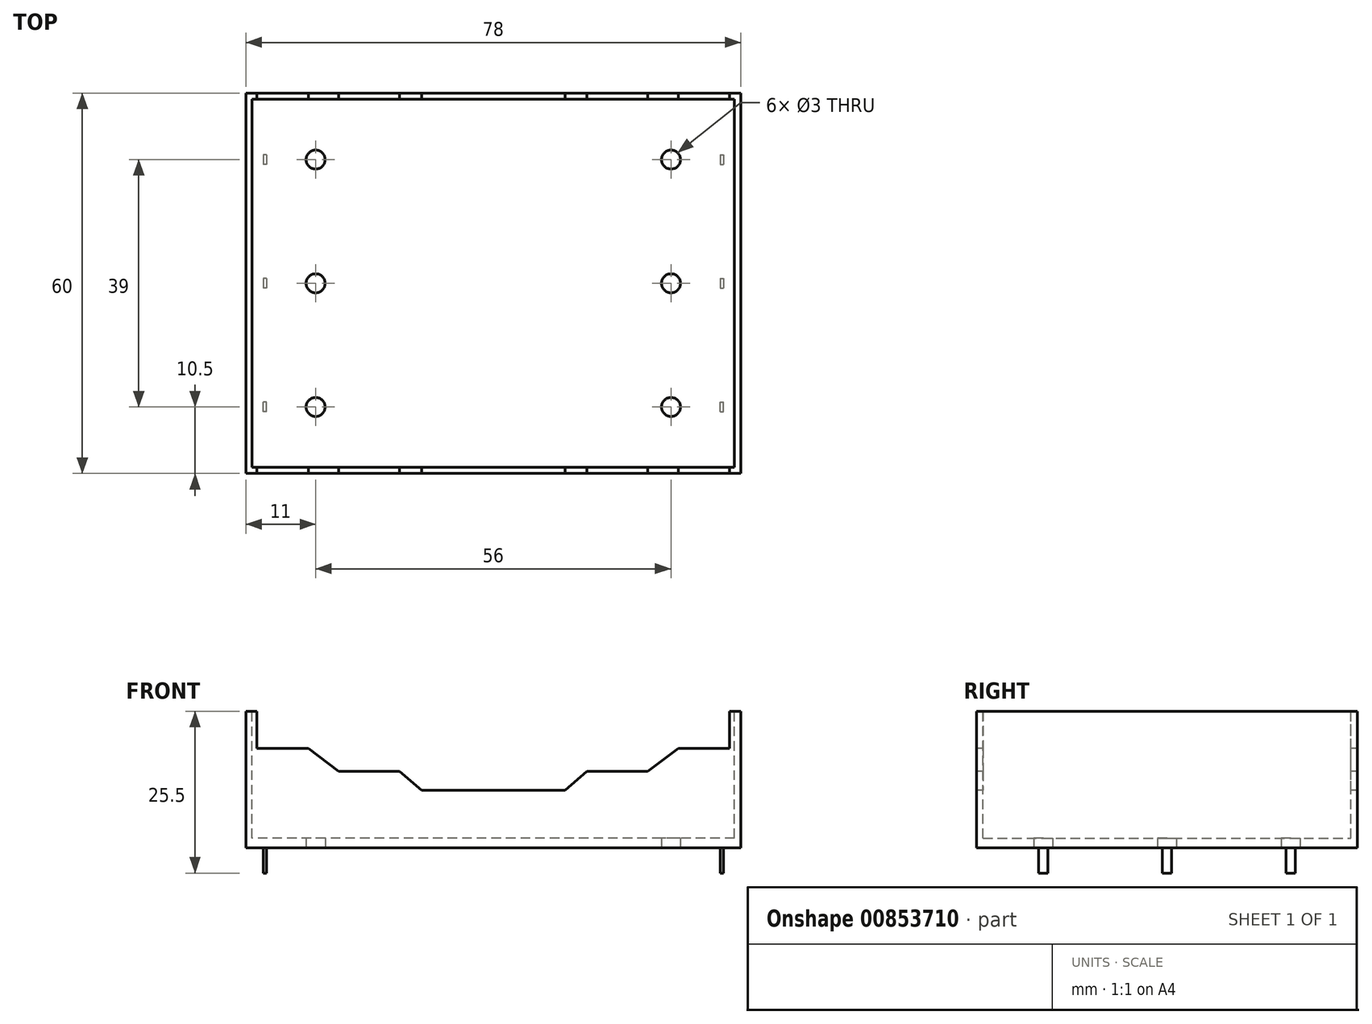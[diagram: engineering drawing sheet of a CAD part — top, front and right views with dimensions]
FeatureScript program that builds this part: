
annotation { "Feature Type Name" : "Feature", "Feature Type Description" : "" }
export const myFeature = defineFeature(function(context is Context, id is Id, definition is map)
    precondition{}
    {
        {
            var Q0;
            Q0=qCreatedBy(makeId("Top.planeOp"),FACE);
            var sketch = newSketch(context, id + "F0", { "sketchPlane" : qUnion([Q0])});
            skLineSegment(sketch, "E0.bottom", {"start": v(0, 0) * mm, "end": v(78, 0) * mm});
            skLineSegment(sketch, "E0.top", {"start": v(0, -60) * mm, "end": v(78, -60) * mm});
            skLineSegment(sketch, "E0.left", {"start": v(0, 0) * mm, "end": v(0, -60) * mm});
            skLineSegment(sketch, "E0.right", {"start": v(78, 0) * mm, "end": v(78, -60) * mm});
            skSolve(sketch);
        }
        {
            var Q0;
            Q0 = qSketchRegion(id + "F0", true);
            extrude(context, id + "F1", {"entities" : qUnion([Q0]), "depth" : 21.5 * mm, "offsetDistance" : 25 * mm});
        }
        {
            var Q0;
            Q0=makeQuery(id+"F1.opExtrude","CAP_FACE",FACE,{"disambiguationData":[OSD([sQuery(id+"F0.wireOp",EDGE,"E0.bottom"),sQuery(id+"F0.wireOp",EDGE,"E0.top"),sQuery(id+"F0.wireOp",EDGE,"E0.left"),sQuery(id+"F0.wireOp",EDGE,"E0.right")])],"isStart":false});
            var sketch = newSketch(context, id + "F2", { "sketchPlane" : qUnion([Q0])});
            skLineSegment(sketch, "E1.0.0", {"start": v(0, 0) * mm, "end": v(0, -60) * mm});
            skLineSegment(sketch, "E1.0.1", {"start": v(0, -60) * mm, "end": v(78, -60) * mm});
            skLineSegment(sketch, "E1.0.2", {"start": v(78, -60) * mm, "end": v(78, 0) * mm});
            skLineSegment(sketch, "E1.0.3", {"start": v(78, 0) * mm, "end": v(0, 0) * mm});
            skLineSegment(sketch, "E2.0", {"start": v(77, -1) * mm, "end": v(1, -1) * mm});
            skLineSegment(sketch, "E2.1", {"start": v(77, -59) * mm, "end": v(77, -1) * mm});
            skLineSegment(sketch, "E2.2", {"start": v(1, -59) * mm, "end": v(77, -59) * mm});
            skLineSegment(sketch, "E2.3", {"start": v(1, -1) * mm, "end": v(1, -59) * mm});
            skSolve(sketch);
        }
        {
            var Q0;
            Q0=makeQuery(id+"F2.imprint","IMPRINT",FACE,{"disambiguationData":[TD([[makeQuery(id+"F2.imprint","IMPRINT",EDGE,{"derivedFrom":sQuery(id+"F2.wireOp",EDGE,"E2.0")}),1.0]])]});
            extrude(context, id + "F3", {"entities" : qUnion([Q0]), "operationType" : NewBodyOperationType.REMOVE, "oppositeDirection" : true, "depth" : 20 * mm, "offsetDistance" : 25 * mm});
        }
        {
            var Q0;
            Q0=makeQuery(id+"F1.opExtrude","SWEPT_FACE",FACE,{"disambiguationData":[OSD([sQuery(id+"F0.wireOp",EDGE,"E0.top")])]});
            var sketch = newSketch(context, id + "F4", { "sketchPlane" : qUnion([Q0])});
            skLineSegment(sketch, "E3", {"start": v(39, 21.5) * mm, "end": v(39, 0) * mm, "construction": true});
            skLineSegment(sketch, "E4.0.0", {"start": v(0, 0) * mm, "end": v(39, 0) * mm});
            skLineSegment(sketch, "E4.0.3", {"start": v(0, 21.5) * mm, "end": v(0, 0) * mm});
            skLineSegment(sketch, "E5", {"start": v(1.77, 21.5) * mm, "end": v(1.77, 15.66) * mm});
            skLineSegment(sketch, "E6", {"start": v(1.77, 15.66) * mm, "end": v(9.86, 15.66) * mm});
            skLineSegment(sketch, "E7", {"start": v(9.86, 15.66) * mm, "end": v(14.65, 12.02) * mm});
            skLineSegment(sketch, "E8", {"start": v(14.65, 12.02) * mm, "end": v(24.24, 12.02) * mm});
            skLineSegment(sketch, "E9", {"start": v(24.24, 12.02) * mm, "end": v(27.7, 9.05) * mm});
            skLineSegment(sketch, "E10", {"start": v(27.7, 9.05) * mm, "end": v(39, 9.05) * mm});
            skLineSegment(sketch, "E11", {"start": v(39, 9.05) * mm, "end": v(39, 0) * mm});
            skLineSegment(sketch, "E12.trimOffspring", {"start": v(1.77, 21.5) * mm, "end": v(0, 21.5) * mm});
            skPoint(sketch, "E4.0.1.end.orphan", {"position": v(78, 21.5) * mm});
            skPoint(sketch, "E4.0.1.start.orphan", {"position": v(78, 0) * mm});
            skLineSegment(sketch, "E13.MirrorCS", {"start": v(53.76, 12.02) * mm, "end": v(50.3, 9.05) * mm});
            skLineSegment(sketch, "E14.MirrorCS", {"start": v(76.23, 21.5) * mm, "end": v(78, 21.5) * mm});
            skLineSegment(sketch, "E15.MirrorCS", {"start": v(78, 0) * mm, "end": v(39, 0) * mm});
            skLineSegment(sketch, "E16.MirrorCS", {"start": v(68.14, 15.66) * mm, "end": v(63.35, 12.02) * mm});
            skLineSegment(sketch, "E17.MirrorCS", {"start": v(63.35, 12.02) * mm, "end": v(53.76, 12.02) * mm});
            skLineSegment(sketch, "E18.MirrorCS", {"start": v(76.23, 21.5) * mm, "end": v(76.23, 15.66) * mm});
            skLineSegment(sketch, "E19.MirrorCS", {"start": v(76.23, 15.66) * mm, "end": v(68.14, 15.66) * mm});
            skLineSegment(sketch, "E20.MirrorCS", {"start": v(50.3, 9.05) * mm, "end": v(39, 9.05) * mm});
            skLineSegment(sketch, "E21.MirrorCS", {"start": v(78, 21.5) * mm, "end": v(78, 0) * mm});
            skSolve(sketch);
        }
        {
            var Q0;
            {var subQ0=sQuery(id+"F4.wireOp",EDGE,"E5");Q0=makeQuery(id+"F4.imprint","IMPRINT",FACE,{"disambiguationData":[TD([[makeQuery(id+"F4.imprint","IMPRINT",EDGE,{"derivedFrom":subQ0}),1.0]])]});}
            extrude(context, id + "F5", {"entities" : qUnion([Q0]), "operationType" : NewBodyOperationType.REMOVE, "endBound" : BoundingType.THROUGH_ALL, "oppositeDirection" : true, "depth" : 25 * mm, "offsetDistance" : 25 * mm});
        }
        {
            var Q0;
            Q0=makeQuery(id+"F1.opExtrude","CAP_FACE",FACE,{"disambiguationData":[OSD([sQuery(id+"F0.wireOp",EDGE,"E0.bottom"),sQuery(id+"F0.wireOp",EDGE,"E0.top"),sQuery(id+"F0.wireOp",EDGE,"E0.left"),sQuery(id+"F0.wireOp",EDGE,"E0.right")])],"isStart":true});
            var sketch = newSketch(context, id + "F6", { "sketchPlane" : qUnion([Q0])});
            skLineSegment(sketch, "E22", {"start": v(78, 30) * mm, "end": v(0, 30) * mm, "construction": true});
            skLineSegment(sketch, "E23", {"start": v(78, 10.5) * mm, "end": v(0, 10.5) * mm, "construction": true});
            skLineSegment(sketch, "E24", {"start": v(75, 60) * mm, "end": v(75, 0) * mm, "construction": true});
            skLineSegment(sketch, "E25", {"start": v(39, 60) * mm, "end": v(39, 0) * mm, "construction": true});
            skLineSegment(sketch, "E26.bottom", {"start": v(74.75, 9.75) * mm, "end": v(75.25, 9.75) * mm});
            skLineSegment(sketch, "E26.top", {"start": v(74.75, 11.25) * mm, "end": v(75.25, 11.25) * mm});
            skLineSegment(sketch, "E26.left", {"start": v(74.75, 9.75) * mm, "end": v(74.75, 11.25) * mm});
            skLineSegment(sketch, "E26.right", {"start": v(75.25, 9.75) * mm, "end": v(75.25, 11.25) * mm});
            skPoint(sketch, "E26.middle", {"position": v(75, 10.5) * mm});
            skLineSegment(sketch, "E27.bottom", {"start": v(74.75, 29.25) * mm, "end": v(75.25, 29.25) * mm});
            skLineSegment(sketch, "E27.top", {"start": v(74.75, 30.75) * mm, "end": v(75.25, 30.75) * mm});
            skLineSegment(sketch, "E27.left", {"start": v(74.75, 29.25) * mm, "end": v(74.75, 30.75) * mm});
            skLineSegment(sketch, "E27.right", {"start": v(75.25, 29.25) * mm, "end": v(75.25, 30.75) * mm});
            skPoint(sketch, "E27.middle", {"position": v(75, 30) * mm});
            skPoint(sketch, "E28.MirrorP", {"position": v(75, 49.5) * mm});
            skLineSegment(sketch, "E29.MirrorCS", {"start": v(74.75, 50.25) * mm, "end": v(74.75, 48.75) * mm});
            skLineSegment(sketch, "E30.MirrorCS", {"start": v(74.75, 48.75) * mm, "end": v(75.25, 48.75) * mm});
            skLineSegment(sketch, "E31.MirrorCS", {"start": v(74.75, 50.25) * mm, "end": v(75.25, 50.25) * mm});
            skLineSegment(sketch, "E32.MirrorCS", {"start": v(75.25, 50.25) * mm, "end": v(75.25, 48.75) * mm});
            skLineSegment(sketch, "E33.MirrorCS", {"start": v(2.75, 9.75) * mm, "end": v(2.75, 11.25) * mm});
            skLineSegment(sketch, "E34.MirrorCS", {"start": v(3.25, 9.75) * mm, "end": v(3.25, 11.25) * mm});
            skLineSegment(sketch, "E35.MirrorCS", {"start": v(3.25, 11.25) * mm, "end": v(2.75, 11.25) * mm});
            skLineSegment(sketch, "E36.MirrorCS", {"start": v(3.25, 50.25) * mm, "end": v(3.25, 48.75) * mm});
            skLineSegment(sketch, "E37.MirrorCS", {"start": v(2.75, 50.25) * mm, "end": v(2.75, 48.75) * mm});
            skLineSegment(sketch, "E38.MirrorCS", {"start": v(3.25, 9.75) * mm, "end": v(2.75, 9.75) * mm});
            skLineSegment(sketch, "E39.MirrorCS", {"start": v(3.25, 30.75) * mm, "end": v(2.75, 30.75) * mm});
            skLineSegment(sketch, "E40.MirrorCS", {"start": v(2.75, 29.25) * mm, "end": v(2.75, 30.75) * mm});
            skLineSegment(sketch, "E41.MirrorCS", {"start": v(3.25, 29.25) * mm, "end": v(3.25, 30.75) * mm});
            skLineSegment(sketch, "E42.MirrorCS", {"start": v(3.25, 29.25) * mm, "end": v(2.75, 29.25) * mm});
            skLineSegment(sketch, "E43.MirrorCS", {"start": v(3.25, 48.75) * mm, "end": v(2.75, 48.75) * mm});
            skLineSegment(sketch, "E44.MirrorCS", {"start": v(3.25, 50.25) * mm, "end": v(2.75, 50.25) * mm});
            skPoint(sketch, "E45.MirrorP", {"position": v(3, 49.5) * mm});
            skPoint(sketch, "E46.MirrorP", {"position": v(3, 30) * mm});
            skPoint(sketch, "E47.MirrorP", {"position": v(3, 10.5) * mm});
            skSolve(sketch);
        }
        {
            var Q0;
            Q0 = qSketchRegion(id + "F6", true);
            extrude(context, id + "F7", {"entities" : qUnion([Q0]), "operationType" : NewBodyOperationType.ADD, "depth" : 4 * mm, "offsetDistance" : 25 * mm});
        }
        {
            var Q0;
            Q0=makeQuery(id+"F1.opExtrude","CAP_FACE",FACE,{"disambiguationData":[OSD([sQuery(id+"F0.wireOp",EDGE,"E0.bottom"),sQuery(id+"F0.wireOp",EDGE,"E0.top"),sQuery(id+"F0.wireOp",EDGE,"E0.left"),sQuery(id+"F0.wireOp",EDGE,"E0.right")])],"isStart":true});
            var sketch = newSketch(context, id + "F8", { "sketchPlane" : qUnion([Q0])});
            skLineSegment(sketch, "E48.0", {"start": v(78, 10.5) * mm, "end": v(0, 10.5) * mm});
            skLineSegment(sketch, "E49.0", {"start": v(78, 30) * mm, "end": v(0, 30) * mm});
            skLineSegment(sketch, "E50", {"start": v(67, 60) * mm, "end": v(67, 0) * mm, "construction": true});
            skCircle(sketch, "E51", {"center": v(67, 10.5) * mm, "radius": 1.5 * mm});
            skCircle(sketch, "E52", {"center": v(67, 30) * mm, "radius": 1.5 * mm});
            skCircle(sketch, "E53.MirrorC", {"center": v(67, 49.5) * mm, "radius": 1.5 * mm});
            skCircle(sketch, "E54.MirrorC", {"center": v(11, 49.5) * mm, "radius": 1.5 * mm});
            skCircle(sketch, "E55.MirrorC", {"center": v(11, 10.5) * mm, "radius": 1.5 * mm});
            skCircle(sketch, "E56.MirrorC", {"center": v(11, 30) * mm, "radius": 1.5 * mm});
            skSolve(sketch);
        }
        {
            var Q0;
            Q0 = qSketchRegion(id + "F8", true);
            extrude(context, id + "F9", {"entities" : qUnion([Q0]), "operationType" : NewBodyOperationType.REMOVE, "oppositeDirection" : true, "depth" : 25 * mm, "offsetDistance" : 25 * mm});
        }
    });
